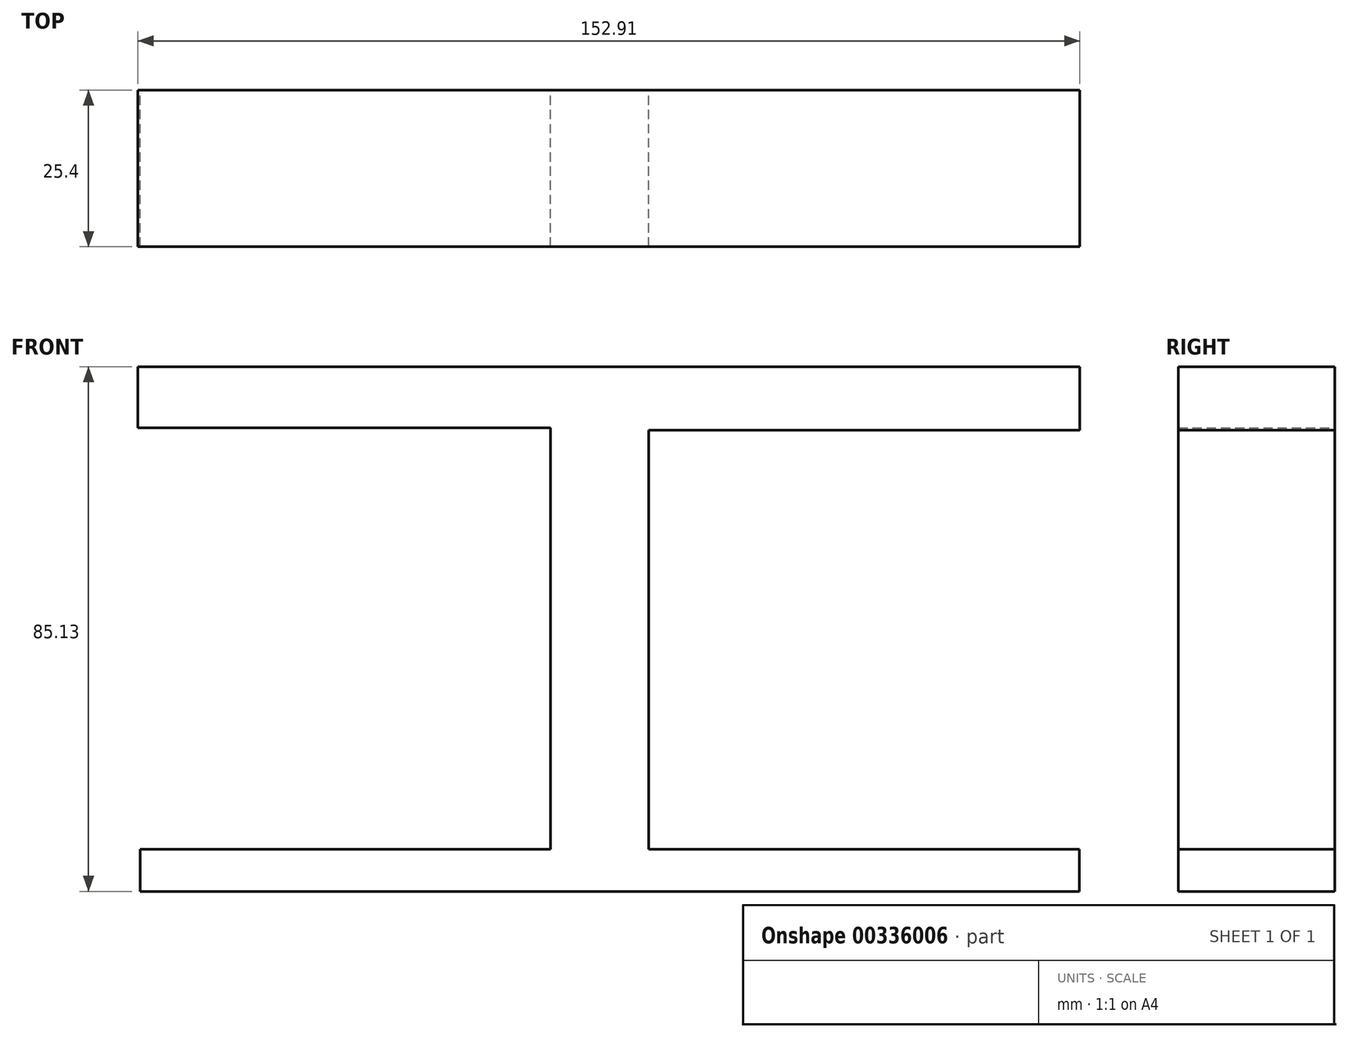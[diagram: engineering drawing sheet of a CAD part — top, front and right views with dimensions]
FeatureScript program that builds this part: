
annotation { "Feature Type Name" : "Feature", "Feature Type Description" : "" }
export const myFeature = defineFeature(function(context is Context, id is Id, definition is map)
    precondition{}
    {
        {
            var Q0;
            Q0=qCreatedBy(makeId("Front.planeOp"),FACE);
            var sketch = newSketch(context, id + "F0", { "sketchPlane" : qUnion([Q0])});
            skLineSegment(sketch, "E0", {"start": v(-76.46, 57.58) * mm, "end": v(76.45, 57.58) * mm});
            skLineSegment(sketch, "E1", {"start": v(76.45, 57.58) * mm, "end": v(76.45, 47.28) * mm});
            skLineSegment(sketch, "E2", {"start": v(76.45, 47.28) * mm, "end": v(6.47, 47.28) * mm});
            skLineSegment(sketch, "E3", {"start": v(-9.5, 47.68) * mm, "end": v(-76.46, 47.68) * mm});
            skLineSegment(sketch, "E4", {"start": v(-76.46, 47.68) * mm, "end": v(-76.46, 57.58) * mm});
            skLineSegment(sketch, "E5", {"start": v(6.47, 47.28) * mm, "end": v(6.47, -20.71) * mm});
            skLineSegment(sketch, "E6", {"start": v(6.47, -20.71) * mm, "end": v(76.38, -20.71) * mm});
            skLineSegment(sketch, "E7", {"start": v(76.38, -20.71) * mm, "end": v(76.38, -27.55) * mm});
            skLineSegment(sketch, "E8", {"start": v(76.38, -27.55) * mm, "end": v(-76.11, -27.55) * mm});
            skLineSegment(sketch, "E9", {"start": v(-76.11, -27.55) * mm, "end": v(-76.11, -20.71) * mm});
            skLineSegment(sketch, "E10", {"start": v(-76.11, -20.71) * mm, "end": v(-9.5, -20.71) * mm});
            skLineSegment(sketch, "E11", {"start": v(-9.5, -20.71) * mm, "end": v(-9.5, 47.68) * mm});
            skSolve(sketch);
        }
        {
            var Q0;
            Q0 = qSketchRegion(id + "F0", true);
            extrude(context, id + "F1", {"entities" : qUnion([Q0]), "depth" : 25.4 * mm});
        }
    });
